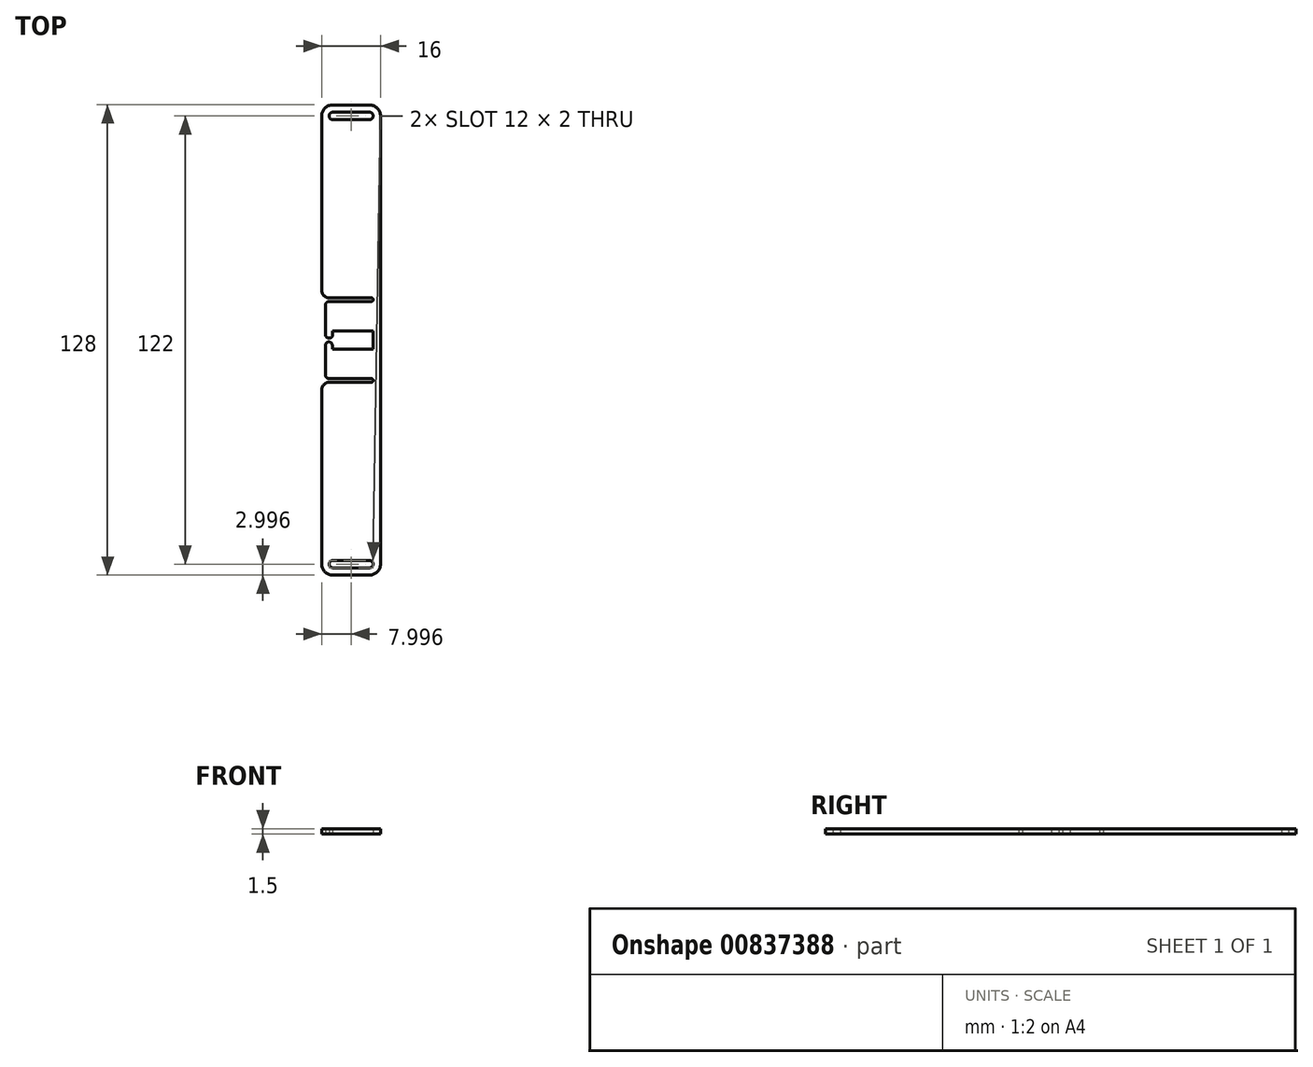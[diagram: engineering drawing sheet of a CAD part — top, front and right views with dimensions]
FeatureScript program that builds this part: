
annotation { "Feature Type Name" : "Feature", "Feature Type Description" : "" }
export const myFeature = defineFeature(function(context is Context, id is Id, definition is map)
    precondition{}
    {
        {
            var Q0;
            Q0=qCreatedBy(makeId("Top.planeOp"),FACE);
            var sketch = newSketch(context, id + "F0", { "sketchPlane" : qUnion([Q0])});
            skLineSegment(sketch, "E0.bottom", {"start": v(-4.76, 27.28) * mm, "end": v(6.74, 27.28) * mm});
            skLineSegment(sketch, "E0.top", {"start": v(-4.76, 17.28) * mm, "end": v(-3.76, 17.28) * mm});
            skLineSegment(sketch, "E0.left", {"start": v(-5.76, 26.28) * mm, "end": v(-5.76, 18.28) * mm});
            skLineSegment(sketch, "E1.bottom", {"start": v(-4.76, 16.28) * mm, "end": v(-3.89, 16.28) * mm});
            skLineSegment(sketch, "E1.top", {"start": v(-4.76, 6.28) * mm, "end": v(6.74, 6.28) * mm});
            skLineSegment(sketch, "E1.left", {"start": v(-5.76, 15.28) * mm, "end": v(-5.76, 7.28) * mm});
            skLineSegment(sketch, "E2.bottom", {"start": v(6.74, 28.28) * mm, "end": v(-5.76, 28.28) * mm});
            skLineSegment(sketch, "E2.left", {"start": v(7.24, 27.78) * mm, "end": v(7.24, 27.78) * mm});
            skLineSegment(sketch, "E3.top", {"start": v(6.74, 5.28) * mm, "end": v(-5.76, 5.28) * mm});
            skLineSegment(sketch, "E4.trimOffspring", {"start": v(7.24, 5.78) * mm, "end": v(7.24, 5.78) * mm});
            skLineSegment(sketch, "E5.bottom", {"start": v(-3.76, -43.22) * mm, "end": v(6.24, -43.22) * mm});
            skLineSegment(sketch, "E5.top", {"start": v(-3.76, -45.22) * mm, "end": v(6.24, -45.22) * mm});
            skLineSegment(sketch, "E5.left", {"start": v(-4.76, -44.22) * mm, "end": v(-4.76, -44.22) * mm});
            skLineSegment(sketch, "E5.right", {"start": v(7.24, -44.22) * mm, "end": v(7.24, -44.22) * mm});
            skLineSegment(sketch, "E6.bottom", {"start": v(-3.76, 76.78) * mm, "end": v(6.24, 76.78) * mm});
            skLineSegment(sketch, "E6.top", {"start": v(-3.76, 78.78) * mm, "end": v(6.24, 78.78) * mm});
            skLineSegment(sketch, "E6.left", {"start": v(-4.76, 77.78) * mm, "end": v(-4.76, 77.78) * mm});
            skLineSegment(sketch, "E6.right", {"start": v(7.24, 77.78) * mm, "end": v(7.24, 77.78) * mm});
            skPoint(sketch, "E7.visualSharp", {"position": v(-5.76, 27.28) * mm});
            skArc(sketch, "E7.filletArc", {"start": v(-4.76, 27.28) * mm, "mid": v(-5.47, 26.98) * mm, "end": v(-5.76, 26.28) * mm});
            skPoint(sketch, "E8.visualSharp", {"position": v(-5.76, 17.28) * mm});
            skArc(sketch, "E8.filletArc", {"start": v(-5.76, 18.28) * mm, "mid": v(-5.47, 17.57) * mm, "end": v(-4.76, 17.28) * mm});
            skPoint(sketch, "E9.visualSharp", {"position": v(-6.76, 16.78) * mm});
            skPoint(sketch, "E10.visualSharp", {"position": v(-6.76, 28.28) * mm});
            skPoint(sketch, "E11.visualSharp", {"position": v(-5.76, 6.28) * mm});
            skArc(sketch, "E11.filletArc", {"start": v(-5.76, 7.28) * mm, "mid": v(-5.47, 6.57) * mm, "end": v(-4.76, 6.28) * mm});
            skPoint(sketch, "E12.visualSharp", {"position": v(-6.76, 5.28) * mm});
            skPoint(sketch, "E13.visualSharp", {"position": v(-6.76, 17.28) * mm});
            skPoint(sketch, "E14.visualSharp", {"position": v(-5.76, 16.28) * mm});
            skArc(sketch, "E14.filletArc", {"start": v(-4.76, 16.28) * mm, "mid": v(-5.47, 15.98) * mm, "end": v(-5.76, 15.28) * mm});
            skPoint(sketch, "E15.visualSharp", {"position": v(7.24, 16.28) * mm});
            skPoint(sketch, "E16.visualSharp", {"position": v(7.24, 16.78) * mm});
            skPoint(sketch, "E17.visualSharp", {"position": v(7.24, 5.28) * mm});
            skArc(sketch, "E17.filletArc", {"start": v(6.74, 5.28) * mm, "mid": v(7.09, 5.42) * mm, "end": v(7.24, 5.78) * mm});
            skPoint(sketch, "E18.visualSharp", {"position": v(7.24, 6.28) * mm});
            skArc(sketch, "E18.filletArc", {"start": v(7.24, 5.78) * mm, "mid": v(7.09, 6.13) * mm, "end": v(6.74, 6.28) * mm});
            skPoint(sketch, "E19.visualSharp", {"position": v(7.24, 27.28) * mm});
            skArc(sketch, "E19.filletArc", {"start": v(6.74, 27.28) * mm, "mid": v(7.09, 27.42) * mm, "end": v(7.24, 27.78) * mm});
            skPoint(sketch, "E20.visualSharp", {"position": v(7.24, 28.28) * mm});
            skArc(sketch, "E20.filletArc", {"start": v(7.24, 27.78) * mm, "mid": v(7.09, 28.13) * mm, "end": v(6.74, 28.28) * mm});
            skPoint(sketch, "E21.visualSharp", {"position": v(7.24, 17.28) * mm});
            skPoint(sketch, "E22.visualSharp", {"position": v(7.24, -43.22) * mm});
            skArc(sketch, "E22.filletArc", {"start": v(7.24, -44.22) * mm, "mid": v(6.94, -43.52) * mm, "end": v(6.24, -43.22) * mm});
            skPoint(sketch, "E23.visualSharp", {"position": v(7.24, -45.22) * mm});
            skArc(sketch, "E23.filletArc", {"start": v(6.24, -45.22) * mm, "mid": v(6.94, -44.93) * mm, "end": v(7.24, -44.22) * mm});
            skPoint(sketch, "E24.visualSharp", {"position": v(-4.76, -45.22) * mm});
            skArc(sketch, "E24.filletArc", {"start": v(-4.76, -44.22) * mm, "mid": v(-4.47, -44.93) * mm, "end": v(-3.76, -45.22) * mm});
            skPoint(sketch, "E25.visualSharp", {"position": v(-4.76, -43.22) * mm});
            skArc(sketch, "E25.filletArc", {"start": v(-3.76, -43.22) * mm, "mid": v(-4.47, -43.52) * mm, "end": v(-4.76, -44.22) * mm});
            skPoint(sketch, "E26.visualSharp", {"position": v(-4.76, 78.78) * mm});
            skArc(sketch, "E26.filletArc", {"start": v(-3.76, 78.78) * mm, "mid": v(-4.47, 78.48) * mm, "end": v(-4.76, 77.78) * mm});
            skPoint(sketch, "E27.visualSharp", {"position": v(-4.76, 76.78) * mm});
            skArc(sketch, "E27.filletArc", {"start": v(-4.76, 77.78) * mm, "mid": v(-4.47, 77.07) * mm, "end": v(-3.76, 76.78) * mm});
            skPoint(sketch, "E28.visualSharp", {"position": v(7.24, 76.78) * mm});
            skArc(sketch, "E28.filletArc", {"start": v(6.24, 76.78) * mm, "mid": v(6.94, 77.07) * mm, "end": v(7.24, 77.78) * mm});
            skPoint(sketch, "E29.visualSharp", {"position": v(7.24, 78.78) * mm});
            skArc(sketch, "E29.filletArc", {"start": v(7.24, 77.78) * mm, "mid": v(6.94, 78.48) * mm, "end": v(6.24, 78.78) * mm});
            skPoint(sketch, "E30.left.end.orphan", {"position": v(-13.76, 9.78) * mm});
            skPoint(sketch, "E30.left.start.orphan", {"position": v(-13.76, 24.78) * mm});
            skPoint(sketch, "E31.start.orphan", {"position": v(-13.76, 61.78) * mm});
            skPoint(sketch, "E32.bottom.start.orphan", {"position": v(-13.76, 84.78) * mm});
            skPoint(sketch, "E33.start.orphan", {"position": v(16.24, 61.78) * mm});
            skPoint(sketch, "E34.start.orphan", {"position": v(-7.76, 24.78) * mm});
            skPoint(sketch, "E35.start.orphan", {"position": v(10.24, 24.78) * mm});
            skPoint(sketch, "E36.start.orphan", {"position": v(-7.76, 9.78) * mm});
            skPoint(sketch, "E37.start.orphan", {"position": v(10.24, 9.78) * mm});
            skPoint(sketch, "E38.trimOffspring.start.orphan", {"position": v(16.24, -28.22) * mm});
            skPoint(sketch, "E39.trimOffspring.start.orphan", {"position": v(-13.76, -28.22) * mm});
            skPoint(sketch, "E32.top.start.orphan", {"position": v(-13.76, -50.22) * mm});
            skLineSegment(sketch, "E40.top", {"start": v(7.24, 19.28) * mm, "end": v(-3.76, 19.28) * mm});
            skLineSegment(sketch, "E40.left", {"start": v(7.24, 17.28) * mm, "end": v(7.24, 19.28) * mm});
            skLineSegment(sketch, "E40.right", {"start": v(-3.76, 17.28) * mm, "end": v(-3.76, 19.28) * mm});
            skPoint(sketch, "E41.right.end.orphan", {"position": v(-4.07, 15.28) * mm});
            skLineSegment(sketch, "E42.top", {"start": v(-3.89, 14.28) * mm, "end": v(7.24, 14.28) * mm});
            skLineSegment(sketch, "E42.left", {"start": v(-3.89, 16.28) * mm, "end": v(-3.89, 14.28) * mm});
            skLineSegment(sketch, "E42.right", {"start": v(7.24, 16.28) * mm, "end": v(7.24, 14.28) * mm});
            skLineSegment(sketch, "E43", {"start": v(7.24, 17.28) * mm, "end": v(7.24, 16.28) * mm});
            skLineSegment(sketch, "E44.bottom", {"start": v(-6.76, 80.78) * mm, "end": v(9.24, 80.78) * mm});
            skLineSegment(sketch, "E44.top", {"start": v(-6.76, -47.22) * mm, "end": v(9.24, -47.22) * mm});
            skLineSegment(sketch, "E44.left", {"start": v(-6.76, 80.78) * mm, "end": v(-6.76, 16.78) * mm});
            skLineSegment(sketch, "E44.right", {"start": v(9.24, 80.78) * mm, "end": v(9.24, -47.22) * mm});
            skLineSegment(sketch, "E45", {"start": v(-5.76, 28.28) * mm, "end": v(-6.76, 28.28) * mm});
            skLineSegment(sketch, "E46", {"start": v(-5.76, 5.28) * mm, "end": v(-6.76, 5.28) * mm});
            skLineSegment(sketch, "E47.trimOffspring", {"start": v(-6.76, 5.28) * mm, "end": v(-6.76, -47.22) * mm});
            skSolve(sketch);
        }
        {
            var Q0;
            Q0=qSketchRegion(id+"F0",true);
            extrude(context, id + "F1", {"entities" : qUnion([Q0]), "depth" : 1.5 * mm, "offsetDistance" : 25 * mm});
        }
        {
            var Q0;
            Q0=makeQuery(id+"F1.opExtrude","SWEPT_EDGE",EDGE,{"disambiguationData":[OSD([sQuery(id+"F0.wireOp",EDGE,"E0.top"),sQuery(id+"F0.wireOp",EDGE,"E40.right")])]});
            var Q1;
            Q1=makeQuery(id+"F1.opExtrude","SWEPT_EDGE",EDGE,{"disambiguationData":[OSD([sQuery(id+"F0.wireOp",EDGE,"E1.bottom"),sQuery(id+"F0.wireOp",EDGE,"E42.left")])]});
            fillet(context, id + "F2", {"entities" : qUnion([Q0, Q1]), "radius" : 1 * mm, "tangentPropagation" : true, "allowEdgeOverflow" : false});
        }
        {
            var Q0;
            Q0=makeQuery(id+"F1.opExtrude","SWEPT_EDGE",EDGE,{"disambiguationData":[OSD([sQuery(id+"F0.wireOp",EDGE,"E44.left"),sQuery(id+"F0.wireOp",EDGE,"E45")])]});
            var Q1;
            Q1=makeQuery(id+"F1.opExtrude","SWEPT_EDGE",EDGE,{"disambiguationData":[OSD([sQuery(id+"F0.wireOp",EDGE,"E46"),sQuery(id+"F0.wireOp",EDGE,"E47.trimOffspring")])]});
            fillet(context, id + "F3", {"entities" : qUnion([Q0, Q1]), "radius" : 2 * mm, "tangentPropagation" : true, "allowEdgeOverflow" : false});
        }
        {
            var Q0;
            Q0=makeQuery(id+"F1.opExtrude","SWEPT_EDGE",EDGE,{"disambiguationData":[OSD([sQuery(id+"F0.wireOp",EDGE,"E44.bottom"),sQuery(id+"F0.wireOp",EDGE,"E44.right")])]});
            var Q1;
            Q1=makeQuery(id+"F1.opExtrude","SWEPT_EDGE",EDGE,{"disambiguationData":[OSD([sQuery(id+"F0.wireOp",EDGE,"E44.bottom"),sQuery(id+"F0.wireOp",EDGE,"E44.left")])]});
            var Q2;
            Q2=makeQuery(id+"F1.opExtrude","SWEPT_EDGE",EDGE,{"disambiguationData":[OSD([sQuery(id+"F0.wireOp",EDGE,"E44.top"),sQuery(id+"F0.wireOp",EDGE,"E47.trimOffspring")])]});
            var Q3;
            Q3=makeQuery(id+"F1.opExtrude","SWEPT_EDGE",EDGE,{"disambiguationData":[OSD([sQuery(id+"F0.wireOp",EDGE,"E44.top"),sQuery(id+"F0.wireOp",EDGE,"E44.right")])]});
            fillet(context, id + "F4", {"entities" : qUnion([Q0, Q1, Q2, Q3]), "radius" : 3 * mm, "tangentPropagation" : true, "allowEdgeOverflow" : false});
        }
    });
